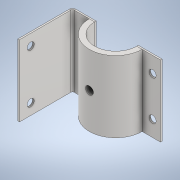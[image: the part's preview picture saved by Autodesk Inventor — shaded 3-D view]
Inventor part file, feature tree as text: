
AUTODESK INVENTOR PART (.ipt)
format: ipt  version: 2020.3 (Build 243373000, 373)  size: 145,920 bytes
history: native  units: in
note: dims shown in document units (in); Inventor stores cm internally (conversion verified against a paired STEP export)
features: other x3, thread x1
ambient origin geometry x8: Origin, YZ Plane, XZ Plane, XY Plane, X Axis, Y Axis, Z Axis, Center Point
bodies: Solid1 (feature_tree), Solid2 (feature_tree), Solid3 (feature_tree)
feature tree (4):
  thread  "Thread1"  [1 undecoded]
  other  "Plate A connector box-iv stand:1"
  other  "Half Pipe A53 - DN25-H45:1"
  other  "Plate B connector box-iv stand:1"
note: 1 required parameter value undecoded (feature->parameter linkage not recoverable at this tier; creation-order binding heuristic only, values carry confidence <= 0.55)
